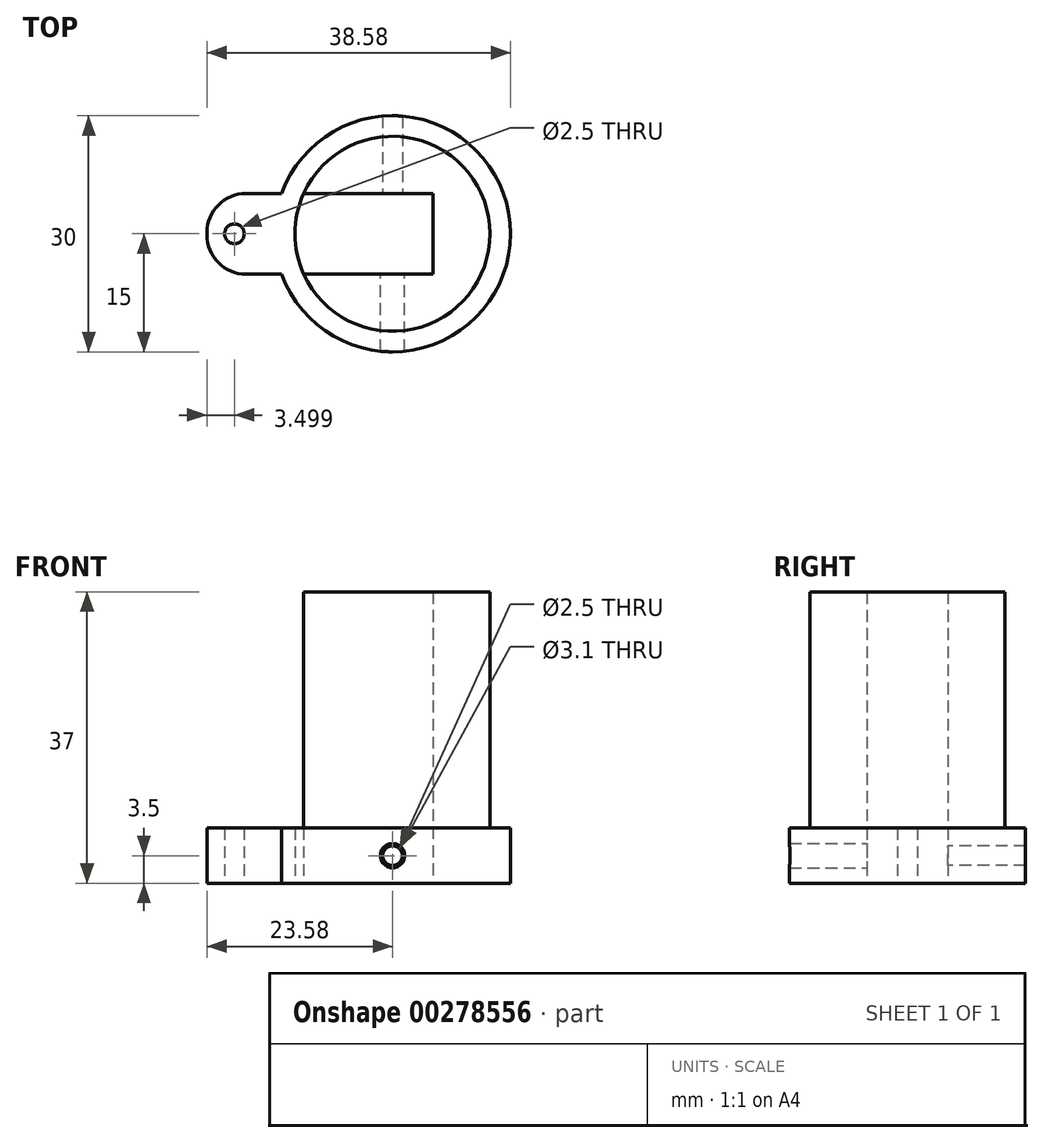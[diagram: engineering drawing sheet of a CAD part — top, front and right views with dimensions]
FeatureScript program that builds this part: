
annotation { "Feature Type Name" : "Feature", "Feature Type Description" : "" }
export const myFeature = defineFeature(function(context is Context, id is Id, definition is map)
    precondition{}
    {
        {
            var Q0;
            Q0=qCreatedBy(makeId("Top.planeOp"),FACE);
            var sketch = newSketch(context, id + "F0", { "sketchPlane" : qUnion([Q0])});
            skCircle(sketch, "E0", {"center": v(0, 0) * mm, "radius": 15 * mm});
            skPoint(sketch, "E1", {"position": v(15, 0) * mm});
            skLineSegment(sketch, "E2.bottom", {"start": v(-5.13, 5.13) * mm, "end": v(5.13, 5.13) * mm});
            skLineSegment(sketch, "E2.top", {"start": v(-5.13, -5.13) * mm, "end": v(5.13, -5.13) * mm});
            skLineSegment(sketch, "E2.left", {"start": v(-5.13, 5.13) * mm, "end": v(-5.13, -5.13) * mm});
            skLineSegment(sketch, "E2.right", {"start": v(5.13, 5.13) * mm, "end": v(5.13, -5.13) * mm});
            skCircle(sketch, "E3", {"center": v(0, 0) * mm, "radius": 12.38 * mm});
            skPoint(sketch, "E4", {"position": v(12.38, 0) * mm});
            skLineSegment(sketch, "E5.bottom", {"start": v(-5.13, -5.13) * mm, "end": v(-5.13, -5.13) * mm});
            skLineSegment(sketch, "E5.top", {"start": v(-5.13, 5.13) * mm, "end": v(-5.13, 5.13) * mm});
            skLineSegment(sketch, "E5.left", {"start": v(-5.13, -5.13) * mm, "end": v(-5.13, 5.13) * mm});
            skLineSegment(sketch, "E5.right", {"start": v(-5.13, -5.13) * mm, "end": v(-5.13, 5.13) * mm});
            skLineSegment(sketch, "E6.bottom", {"start": v(-5.13, -5.13) * mm, "end": v(-23.58, -5.13) * mm});
            skLineSegment(sketch, "E6.top", {"start": v(-5.13, 5.13) * mm, "end": v(-23.58, 5.13) * mm});
            skLineSegment(sketch, "E6.right", {"start": v(-23.58, -5.13) * mm, "end": v(-23.58, 5.13) * mm});
            skLineSegment(sketch, "E7", {"start": v(-23.58, 0) * mm, "end": v(-20.08, 0) * mm});
            skPoint(sketch, "E8", {"position": v(-20.08, 0) * mm});
            skSolve(sketch);
        }
        {
            var Q0;
            {var subQ0=sQuery(id+"F0.wireOp",EDGE,"E6.bottom");var subQ1=sQuery(id+"F0.wireOp",EDGE,"E0");var subQ2=makeQuery(id+"F0.imprint","INTERSECT",VERTEX,{"derivedFrom":[subQ1,subQ0]});Q0=makeQuery(id+"F0.imprint","IMPRINT",FACE,{"disambiguationData":[TD([[makeQuery(id+"F0.imprint","IMPRINT",EDGE,{"disambiguationData":[TD([[subQ2,-1.0]])],"derivedFrom":subQ1}),1.0]])]});}
            var Q1;
            {var subQ0=sQuery(id+"F0.wireOp",EDGE,"E6.bottom");var subQ1=sQuery(id+"F0.wireOp",EDGE,"E0");var subQ2=makeQuery(id+"F0.imprint","INTERSECT",VERTEX,{"derivedFrom":[subQ1,subQ0]});Q1=makeQuery(id+"F0.imprint","IMPRINT",FACE,{"disambiguationData":[TD([[makeQuery(id+"F0.imprint","IMPRINT",EDGE,{"disambiguationData":[TD([[subQ2,1.0]])],"derivedFrom":subQ1}),1.0]])]});}
            var Q2;
            {var subQ6=sQuery(id+"F0.wireOp",EDGE,"E2.bottom");Q2=makeQuery(id+"F0.imprint","IMPRINT",FACE,{"disambiguationData":[TD([[makeQuery(id+"F0.imprint","IMPRINT",EDGE,{"derivedFrom":subQ6}),1.0]])]});}
            var Q3;
            {var subQ5=sQuery(id+"F0.wireOp",EDGE,"E5.left");Q3=makeQuery(id+"F0.imprint","IMPRINT",FACE,{"disambiguationData":[TD([[makeQuery(id+"F0.imprint","IMPRINT",EDGE,{"derivedFrom":subQ5}),1.0]])]});}
            var Q4;
            {var subQ5=sQuery(id+"F0.wireOp",EDGE,"E6.right");Q4=makeQuery(id+"F0.imprint","IMPRINT",FACE,{"disambiguationData":[TD([[makeQuery(id+"F0.imprint","IMPRINT",EDGE,{"derivedFrom":subQ5}),-1.0]])]});}
            extrude(context, id + "F1", {"entities" : qUnion([Q0, Q1, Q2, Q3, Q4]), "depth" : 7 * mm});
        }
        {
            var Q0;
            {var subQ5=sQuery(id+"F0.wireOp",EDGE,"E5.left");Q0=makeQuery(id+"F0.imprint","IMPRINT",FACE,{"disambiguationData":[TD([[makeQuery(id+"F0.imprint","IMPRINT",EDGE,{"derivedFrom":subQ5}),1.0]])]});}
            var Q1;
            {var subQ6=sQuery(id+"F0.wireOp",EDGE,"E2.bottom");Q1=makeQuery(id+"F0.imprint","IMPRINT",FACE,{"disambiguationData":[TD([[makeQuery(id+"F0.imprint","IMPRINT",EDGE,{"derivedFrom":subQ6}),1.0]])]});}
            extrude(context, id + "F2", {"entities" : qUnion([Q0, Q1]), "operationType" : NewBodyOperationType.ADD, "depth" : 37 * mm});
        }
        {
            var Q0;
            {var subQ0=sQuery(id+"F0.wireOp",EDGE,"E2.bottom");Q0=makeQuery(id+"F2.boolean.opBoolean","MERGE",FACE,{"derivedFrom":[makeQuery(id+"F1.opExtrude","SWEPT_FACE",FACE,{"disambiguationData":[OSD([subQ0])]}),makeQuery(id+"F2.opExtrude","SWEPT_FACE",FACE,{"disambiguationData":[OSD([subQ0])]})]});}
            var sketch = newSketch(context, id + "F3", { "sketchPlane" : qUnion([Q0])});
            skLineSegment(sketch, "E9", {"start": v(0, 0) * mm, "end": v(0, 3.5) * mm});
            skLineSegment(sketch, "E10.bottom", {"start": v(0, 0) * mm, "end": v(2.38, 0) * mm});
            skLineSegment(sketch, "E10.top", {"start": v(0, 3.5) * mm, "end": v(2.38, 3.5) * mm});
            skLineSegment(sketch, "E10.right", {"start": v(2.38, 0) * mm, "end": v(2.38, 3.5) * mm});
            skLineSegment(sketch, "E11.bottom", {"start": v(0, 3.5) * mm, "end": v(-2.51, 3.5) * mm});
            skLineSegment(sketch, "E11.top", {"start": v(0, 0) * mm, "end": v(-2.51, 0) * mm});
            skLineSegment(sketch, "E11.left", {"start": v(0, 3.5) * mm, "end": v(0, 0) * mm});
            skLineSegment(sketch, "E11.right", {"start": v(-2.51, 3.5) * mm, "end": v(-2.51, 0) * mm});
            skPoint(sketch, "E12", {"position": v(0, 3.5) * mm});
            skSolve(sketch);
        }
        {
            var Q0;
            Q0=sQuery(id+"F3.wireOp",VERTEX,"E12");
            var Q1;
            Q1=makeQuery(id+"F1.opExtrude","SWEPT_BODY",BODY,{"disambiguationData":[OSD([sQuery(id+"F0.wireOp",EDGE,"E0"),sQuery(id+"F0.wireOp",EDGE,"E2.bottom"),sQuery(id+"F0.wireOp",EDGE,"E2.top"),sQuery(id+"F0.wireOp",EDGE,"E2.right"),sQuery(id+"F0.wireOp",EDGE,"E6.bottom"),sQuery(id+"F0.wireOp",EDGE,"E6.top"),sQuery(id+"F0.wireOp",EDGE,"E5.left"),sQuery(id+"F0.wireOp",EDGE,"E6.right")])]});
            hole(context, id + "F4", {"style" : HoleStyle.SIMPLE, "endStyle" : HoleEndStyle.THROUGH, "holeDiameter" : 2.5 * mm, "tappedDepth" : 12 * mm, "tapClearance" : 3, "startFromSketch" : true, "locations" : qUnion([Q0]), "scope" : qUnion([Q1])});
        }
        {
            var Q0;
            Q0=sQuery(id+"F3.wireOp",VERTEX,"E12");
            var Q1;
            Q1=makeQuery(id+"F1.opExtrude","SWEPT_BODY",BODY,{"disambiguationData":[OSD([sQuery(id+"F0.wireOp",EDGE,"E0"),sQuery(id+"F0.wireOp",EDGE,"E2.bottom"),sQuery(id+"F0.wireOp",EDGE,"E2.top"),sQuery(id+"F0.wireOp",EDGE,"E2.right"),sQuery(id+"F0.wireOp",EDGE,"E6.bottom"),sQuery(id+"F0.wireOp",EDGE,"E6.top"),sQuery(id+"F0.wireOp",EDGE,"E5.left"),sQuery(id+"F0.wireOp",EDGE,"E6.right")])]});
            hole(context, id + "F5", {"style" : HoleStyle.SIMPLE, "endStyle" : HoleEndStyle.THROUGH, "oppositeDirection" : true, "holeDiameter" : 3.1 * mm, "tappedDepth" : 12 * mm, "tapClearance" : 3, "startFromSketch" : true, "locations" : qUnion([Q0]), "scope" : qUnion([Q1])});
        }
        {
            var Q0;
            Q0=makeQuery(id+"F1.opExtrude","SWEPT_EDGE",EDGE,{"disambiguationData":[OSD([sQuery(id+"F0.wireOp",EDGE,"E6.bottom"),sQuery(id+"F0.wireOp",EDGE,"E6.right")])]});
            var Q1;
            Q1=makeQuery(id+"F1.opExtrude","SWEPT_EDGE",EDGE,{"disambiguationData":[OSD([sQuery(id+"F0.wireOp",EDGE,"E6.top"),sQuery(id+"F0.wireOp",EDGE,"E6.right")])]});
            fillet(context, id + "F6", {"entities" : qUnion([Q0, Q1]), "radius" : 5 * mm, "tangentPropagation" : true, "allowEdgeOverflow" : false});
        }
        {
            var Q0;
            Q0=sQuery(id+"F0.wireOp",VERTEX,"E8");
            var Q1;
            Q1=makeQuery(id+"F1.opExtrude","SWEPT_BODY",BODY,{"disambiguationData":[OSD([sQuery(id+"F0.wireOp",EDGE,"E0"),sQuery(id+"F0.wireOp",EDGE,"E2.bottom"),sQuery(id+"F0.wireOp",EDGE,"E2.top"),sQuery(id+"F0.wireOp",EDGE,"E2.right"),sQuery(id+"F0.wireOp",EDGE,"E6.bottom"),sQuery(id+"F0.wireOp",EDGE,"E6.top"),sQuery(id+"F0.wireOp",EDGE,"E5.left"),sQuery(id+"F0.wireOp",EDGE,"E6.right")])]});
            hole(context, id + "F7", {"style" : HoleStyle.SIMPLE, "endStyle" : HoleEndStyle.THROUGH, "oppositeDirection" : true, "holeDiameter" : 2.5 * mm, "tappedDepth" : 12 * mm, "tapClearance" : 3, "startFromSketch" : true, "locations" : qUnion([Q0]), "scope" : qUnion([Q1])});
        }
    });
